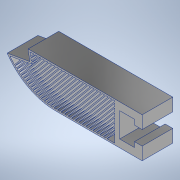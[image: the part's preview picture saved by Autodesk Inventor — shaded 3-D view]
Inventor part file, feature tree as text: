
AUTODESK INVENTOR PART (.ipt)
format: ipt  version: 2022 (Build 260153000, 153)  size: 623,616 bytes
history: native  units: mm
features: extrude x7, sketch x6, fillet x1, shell x1, projected_geometry x1
ambient origin geometry x8: Origin, YZ Plane, XZ Plane, XY Plane, X Axis, Y Axis, Z Axis, Center Point
bodies: Body1 (feature_tree)
feature tree (16):
  extrude  "Extrusion2"  Depth=5.8mm
  extrude  "Extrusion5"  Depth=12.0mm TaperAngle=0.0deg
  fillet  "Fillet2"  Radius=45.0mm
  shell  "Shell1"  Thickness=15.6mm
  extrude  "Extrusion7"  TaperAngle=0.0deg  [1 undecoded]
  extrude  "Extrusion8"  Depth=9.6mm
  extrude  "Extrusion9"  Depth=9.0mm
  extrude  "Extrusion10"  Depth=23.0mm
  extrude  "Extrusion11"  Depth=0.62mm
  sketch  "Sketch8"  dims[d41=5.8mm d48=44.0mm]
  sketch  "Sketch13"  dims[d50=3.0mm d56=12.0mm d57=0.0mm d63=45.0mm d67=15.6mm d71=0.0mm]
  sketch  "Sketch14"  dims[d80=17.453293mm d82=0.0mm d83=0.0mm]
  projected_geometry  "Projected Loop1"
  sketch  "Sketch15"  dims[d87=5.6mm d88=9.6mm]
  sketch  "Sketch16"  dims[d95=4.0mm d96=9.0mm]
  sketch  "Sketch17"  dims[d97=15.6mm d98=23.0mm d99=0.62mm d100=12.0mm d101=0.0mm d102=10.747401mm d103=12.0mm d104=0.0mm d105=0.38mm d107=0.38mm d1=0.38mm d110=0.38mm d111=0.38mm d112=0.38mm d113=0.38mm d127=12.0mm d128=0.0mm d129=0.38mm d131=0.38mm d132=0.38mm d133=0.38mm d134=0.38mm d135=0.38mm d136=0.38mm d137=0.38mm d138=0.38mm d139=0.38mm d151=0.38mm d157=0.38mm d161=0.38mm d163=0.38mm d169=0.38mm d172=0.38mm d174=0.89mm d175=0.38mm d185=22.68928mm d186=22.68928mm d187=22.68928mm d189=0.89mm d200=0.38mm d201=22.68928mm d202=0.89mm d205=0.89mm d206=0.89mm d207=0.89mm d209=0.89mm d210=0.38mm d211=0.38mm d213=0.89mm d214=0.38mm d215=0.38mm d216=0.38mm d217=0.89mm d218=0.89mm d219=12.0mm d220=0.0mm d221=0.89mm d222=0.89mm d223=0.89mm d224=0.38mm d225=0.89mm d226=0.89mm d227=0.89mm d228=0.89mm d229=0.89mm d230=12.0mm d231=0.0mm d232=0.38mm d233=0.89mm d234=0.89mm d235=0.38mm d236=0.89mm d237=0.89mm d238=0.89mm d239=0.89mm d240=0.89mm d241=0.89mm d242=0.89mm d243=0.89mm d244=0.89mm d245=0.89mm d246=0.89mm]
note: 1 required parameter value undecoded (feature->parameter linkage not recoverable at this tier; creation-order binding heuristic only, values carry confidence <= 0.55)
